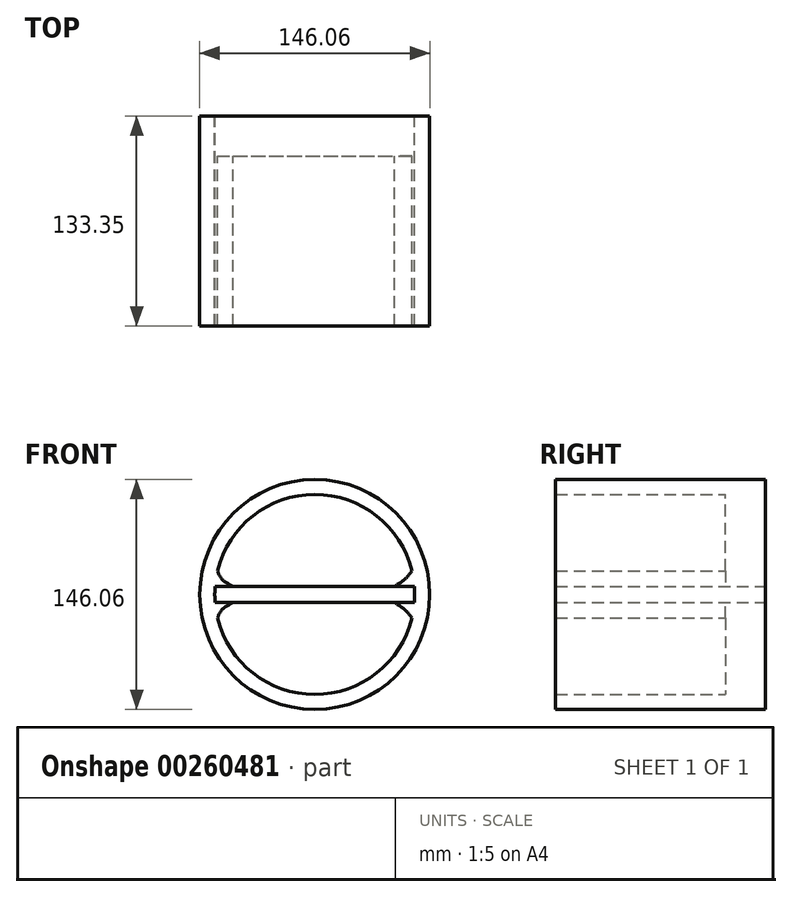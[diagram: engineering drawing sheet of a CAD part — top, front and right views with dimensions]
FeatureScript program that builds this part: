
annotation { "Feature Type Name" : "Feature", "Feature Type Description" : "" }
export const myFeature = defineFeature(function(context is Context, id is Id, definition is map)
    precondition{}
    {
        {
            var Q0;
            Q0=qCreatedBy(makeId("Front.planeOp"),FACE);
            var sketch = newSketch(context, id + "F0", { "sketchPlane" : qUnion([Q0])});
            skCircle(sketch, "E0", {"center": v(0, 0) * mm, "radius": 73.03 * mm});
            skCircle(sketch, "E1", {"center": v(0, 0) * mm, "radius": 63.5 * mm});
            skLineSegment(sketch, "E2", {"start": v(-8.66, 5.08) * mm, "end": v(63.3, 5.08) * mm});
            skLineSegment(sketch, "E3", {"start": v(-63.3, 5.08) * mm, "end": v(-8.66, 5.08) * mm});
            skLineSegment(sketch, "E4", {"start": v(-8.66, -5.08) * mm, "end": v(-63.3, -5.08) * mm});
            skLineSegment(sketch, "E5", {"start": v(-63.3, -5.08) * mm, "end": v(63.3, -5.08) * mm});
            skFitSpline(sketch, "E6", {"points": [v(-61.7, -15.03) * mm, v(-59.18, -9.98) * mm, v(-52, -5.08) * mm], "startDerivative": vector(3.89, 11.87) * mm, "endDerivative": vector(15.03, 8.14) * mm});
            skFitSpline(sketch, "E7", {"points": [v(61.7, -15.03) * mm, v(57.53, -9.98) * mm, v(50.52, -5.08) * mm], "startDerivative": vector(-7.95, 11.2) * mm, "endDerivative": vector(-14.26, 8.74) * mm});
            skFitSpline(sketch, "E8.MirrorCS", {"points": [v(-61.7, 15.03) * mm, v(-59.18, 9.98) * mm, v(-52, 5.08) * mm], "startDerivative": vector(3.89, -11.87) * mm, "endDerivative": vector(15.03, -8.14) * mm});
            skFitSpline(sketch, "E9.MirrorCS", {"points": [v(61.7, 15.03) * mm, v(57.53, 9.98) * mm, v(50.52, 5.08) * mm], "startDerivative": vector(-7.95, -11.2) * mm, "endDerivative": vector(-14.26, -8.74) * mm});
            skSolve(sketch);
        }
        {
            var Q0;
            Q0 = qSketchRegion(id + "F0", true);
            var Q1;
            {var subQ3=sQuery(id+"F0.wireOp",EDGE,"E8.MirrorCS");Q1=makeQuery(id+"F0.imprint","IMPRINT",FACE,{"disambiguationData":[TD([[makeQuery(id+"F0.imprint","IMPRINT",EDGE,{"derivedFrom":subQ3}),-1.0]])]});}
            var Q2;
            {var subQ6=sQuery(id+"F0.wireOp",EDGE,"E5");var subQ13=makeQuery(id+"F0.imprint","IMPRINT",VERTEX,{"derivedFrom":subQ6});Q2=makeQuery(id+"F0.imprint","IMPRINT",FACE,{"disambiguationData":[TD([[makeQuery(id+"F0.imprint","IMPRINT",EDGE,{"disambiguationData":[TD([[subQ13,1.0]])],"derivedFrom":subQ6}),1.0]])]});}
            var Q3;
            {var subQ3=sQuery(id+"F0.wireOp",EDGE,"E6");Q3=makeQuery(id+"F0.imprint","IMPRINT",FACE,{"disambiguationData":[TD([[makeQuery(id+"F0.imprint","IMPRINT",EDGE,{"derivedFrom":subQ3}),1.0]])]});}
            var Q4;
            {var subQ3=sQuery(id+"F0.wireOp",EDGE,"E9.MirrorCS");Q4=makeQuery(id+"F0.imprint","IMPRINT",FACE,{"disambiguationData":[TD([[makeQuery(id+"F0.imprint","IMPRINT",EDGE,{"derivedFrom":subQ3}),1.0]])]});}
            var Q5;
            {var subQ3=sQuery(id+"F0.wireOp",EDGE,"E7");Q5=makeQuery(id+"F0.imprint","IMPRINT",FACE,{"disambiguationData":[TD([[makeQuery(id+"F0.imprint","IMPRINT",EDGE,{"derivedFrom":subQ3}),-1.0]])]});}
            extrude(context, id + "F1", {"entities" : qUnion([Q0, Q1, Q2, Q3, Q4, Q5]), "depth" : 133.35 * mm});
        }
        {
            var Q0;
            {var subQ0=sQuery(id+"F0.wireOp",EDGE,"E8.MirrorCS");Q0=makeQuery(id+"F0.imprint","IMPRINT",FACE,{"disambiguationData":[TD([[makeQuery(id+"F0.imprint","IMPRINT",EDGE,{"derivedFrom":subQ0}),1.0]])]});}
            var Q1;
            {var subQ0=sQuery(id+"F0.wireOp",EDGE,"E6");Q1=makeQuery(id+"F0.imprint","IMPRINT",FACE,{"disambiguationData":[TD([[makeQuery(id+"F0.imprint","IMPRINT",EDGE,{"derivedFrom":subQ0}),-1.0]])]});}
            extrude(context, id + "F2", {"entities" : qUnion([Q0, Q1]), "operationType" : NewBodyOperationType.ADD, "depth" : 25.4 * mm});
        }
    });
